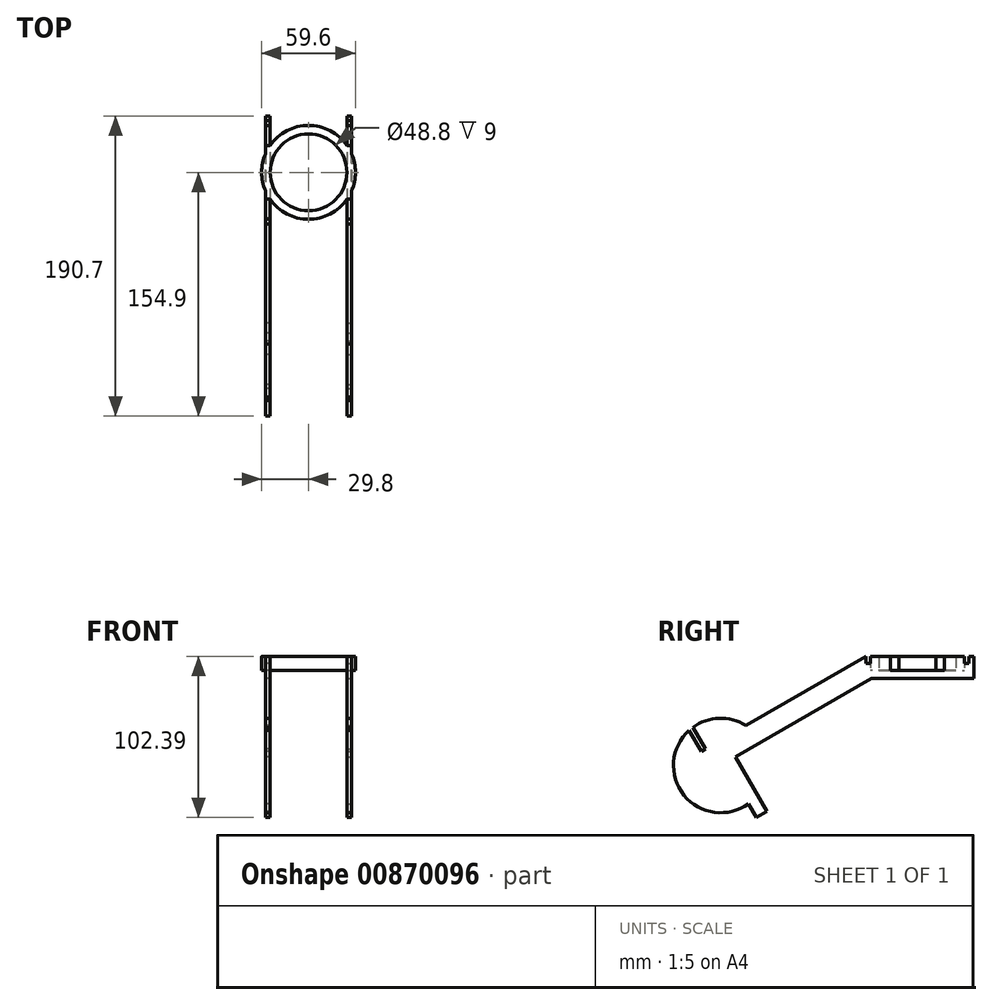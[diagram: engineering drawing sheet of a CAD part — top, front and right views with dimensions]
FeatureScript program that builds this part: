
annotation { "Feature Type Name" : "Feature", "Feature Type Description" : "" }
export const myFeature = defineFeature(function(context is Context, id is Id, definition is map)
    precondition{}
    {
        {
            assignVariable(context, id + "F0", {"name" : "strength", "anyValue" : 3});
        }
        {
            var Q0;
            Q0=qCreatedBy(makeId("Top.planeOp"),FACE);
            var sketch = newSketch(context, id + "F1", { "sketchPlane" : qUnion([Q0])});
            skCircle(sketch, "E0", {"center": v(0, 0) * mm, "radius": 29.8 * mm});
            skCircle(sketch, "E1", {"center": v(0, 0) * mm, "radius": 24.4 * mm});
            skLineSegment(sketch, "E2.bottom", {"start": v(-24.4, -17.1) * mm, "end": v(-27.4, -17.1) * mm});
            skLineSegment(sketch, "E2.top", {"start": v(-24.4, 17.1) * mm, "end": v(-27.4, 17.1) * mm});
            skLineSegment(sketch, "E2.left", {"start": v(-24.4, -17.1) * mm, "end": v(-24.4, 17.1) * mm});
            skLineSegment(sketch, "E2.right", {"start": v(-27.4, -17.1) * mm, "end": v(-27.4, 17.1) * mm});
            skPoint(sketch, "E3", {"position": v(-24.4, -17.1) * mm});
            skPoint(sketch, "E4", {"position": v(-24.4, 17.1) * mm});
            skLineSegment(sketch, "E5.MirrorCS", {"start": v(24.4, 17.1) * mm, "end": v(27.4, 17.1) * mm});
            skLineSegment(sketch, "E6.MirrorCS", {"start": v(27.4, -17.1) * mm, "end": v(27.4, 17.1) * mm});
            skLineSegment(sketch, "E7.MirrorCS", {"start": v(24.4, -17.1) * mm, "end": v(27.4, -17.1) * mm});
            skLineSegment(sketch, "E8.MirrorCS", {"start": v(24.4, -17.1) * mm, "end": v(24.4, 17.1) * mm});
            skSolve(sketch);
        }
        {
            var Q0;
            Q0 = qSketchRegion(id + "F1", true);
            extrude(context, id + "F2", {"entities" : qUnion([Q0]), "depth" : 9 * mm, "offsetDistance" : 25 * mm});
        }
        {
            var Q0;
            {var subQ0=sQuery(id+"F1.wireOp",EDGE,"E2.right");Q0=makeQuery(id+"F2.opExtrude","SWEPT_FACE",FACE,{"disambiguationData":[OSD([subQ0]),TDD([makeQuery(id+"F1.imprint","IMPRINT",EDGE,{"disambiguationData":[TD([[makeQuery(id+"F1.imprint","INTERSECT",VERTEX,{"derivedFrom":[sQuery(id+"F1.wireOp",EDGE,"E2.bottom"),subQ0]}),-1.0]])],"derivedFrom":subQ0})])]});}
            var sketch = newSketch(context, id + "F3", { "sketchPlane" : qUnion([Q0])});
            skLineSegment(sketch, "E9.0", {"start": v(-17.1, 9) * mm, "end": v(-17.1, 0) * mm});
            skLineSegment(sketch, "E10.0", {"start": v(17.1, 9) * mm, "end": v(17.1, 0) * mm});
            skLineSegment(sketch, "E11", {"start": v(-29.8, 0) * mm, "end": v(-29.8, 9) * mm, "construction": true});
            skLineSegment(sketch, "E12", {"start": v(-17.1, 9) * mm, "end": v(-29.8, 9) * mm});
            skLineSegment(sketch, "E13", {"start": v(-29.8, 4.5) * mm, "end": v(-32.8, 4.5) * mm});
            skLineSegment(sketch, "E14", {"start": v(-32.8, 4.5) * mm, "end": v(-32.8, 9) * mm});
            skLineSegment(sketch, "E15", {"start": v(-32.8, 9) * mm, "end": v(-35.8, 9) * mm});
            skLineSegment(sketch, "E16", {"start": v(-35.8, 9) * mm, "end": v(-35.8, 0) * mm});
            skLineSegment(sketch, "E17", {"start": v(-35.8, 0) * mm, "end": v(-35.8, -5) * mm});
            skLineSegment(sketch, "E18", {"start": v(-35.8, -5) * mm, "end": v(29.05, -5) * mm});
            skLineSegment(sketch, "E19", {"start": v(-17.1, 0) * mm, "end": v(0, 0) * mm});
            skLineSegment(sketch, "E20", {"start": v(-29.8, 9) * mm, "end": v(-29.8, 4.5) * mm});
            skLineSegment(sketch, "E21.MirrorCS", {"start": v(17.1, 0) * mm, "end": v(0, 0) * mm});
            skLineSegment(sketch, "E22.MirrorCS", {"start": v(17.1, 9) * mm, "end": v(29.8, 9) * mm});
            skLineSegment(sketch, "E23.MirrorCS", {"start": v(29.8, 4.5) * mm, "end": v(32.8, 4.5) * mm});
            skLineSegment(sketch, "E24.MirrorCS", {"start": v(32.8, 4.5) * mm, "end": v(32.8, 9) * mm});
            skLineSegment(sketch, "E25", {"start": v(29.8, 9) * mm, "end": v(29.8, 4.5) * mm});
            skLineSegment(sketch, "E26", {"start": v(29.05, -5) * mm, "end": v(115.65, -55) * mm});
            skLineSegment(sketch, "E27", {"start": v(115.65, -55) * mm, "end": v(95.65, -89.64) * mm});
            skLineSegment(sketch, "E28", {"start": v(95.65, -89.64) * mm, "end": v(102.15, -93.4) * mm});
            skLineSegment(sketch, "E29", {"start": v(102.15, -93.4) * mm, "end": v(122.15, -58.75) * mm});
            skLineSegment(sketch, "E30", {"start": v(122.15, -58.75) * mm, "end": v(127.65, -61.92) * mm});
            skLineSegment(sketch, "E31", {"start": v(124.9, -60.34) * mm, "end": v(104.9, -94.98) * mm, "construction": true});
            skLineSegment(sketch, "E32", {"start": v(108.92, -34.95) * mm, "end": v(32.8, 9) * mm});
            skLineSegment(sketch, "E33", {"start": v(32.8, 9) * mm, "end": v(32.8, 9) * mm});
            skArc(sketch, "E34", {"start": v(107.23, -84.58) * mm, "mid": v(148.22, -79.2) * mm, "end": v(144.92, -38) * mm});
            skLineSegment(sketch, "E35", {"start": v(127.65, -61.92) * mm, "end": v(134.65, -49.8) * mm, "construction": true});
            skLineSegment(sketch, "E36", {"start": v(108.92, -34.95) * mm, "end": v(134.65, -49.8) * mm, "construction": true});
            skLineSegment(sketch, "E37", {"start": v(134.65, -49.8) * mm, "end": v(142.56, -36.1) * mm});
            skLineSegment(sketch, "E38", {"start": v(134.65, -49.8) * mm, "end": v(137.24, -51.3) * mm});
            skLineSegment(sketch, "E39", {"start": v(137.24, -51.3) * mm, "end": v(144.92, -38) * mm});
            skArc(sketch, "E40.trimOffspring", {"start": v(142.56, -36.1) * mm, "mid": v(118.68, -30.99) * mm, "end": v(98.92, -45.34) * mm});
            skSolve(sketch);
        }
        {
            var Q0;
            Q0 = qSketchRegion(id + "F3", true);
            extrude(context, id + "F4", {"entities" : qUnion([Q0]), "oppositeDirection" : true, "depth" : (getVariable(context, 'strength')) * mm, "offsetDistance" : 25 * mm});
        }
        {
            var Q0;
            Q0=makeQuery(id+"F4.opExtrude","SWEPT_BODY",BODY,{"disambiguationData":[OSD([sQuery(id+"F3.wireOp",EDGE,"E9.0"),sQuery(id+"F3.wireOp",EDGE,"E10.0"),sQuery(id+"F3.wireOp",EDGE,"E12"),sQuery(id+"F3.wireOp",EDGE,"E13"),sQuery(id+"F3.wireOp",EDGE,"E14"),sQuery(id+"F3.wireOp",EDGE,"E15"),sQuery(id+"F3.wireOp",EDGE,"E16"),sQuery(id+"F3.wireOp",EDGE,"E17"),sQuery(id+"F3.wireOp",EDGE,"E18"),sQuery(id+"F3.wireOp",EDGE,"E19"),sQuery(id+"F3.wireOp",EDGE,"E20"),sQuery(id+"F3.wireOp",EDGE,"E21.MirrorCS"),sQuery(id+"F3.wireOp",EDGE,"E22.MirrorCS"),sQuery(id+"F3.wireOp",EDGE,"E23.MirrorCS"),sQuery(id+"F3.wireOp",EDGE,"E24.MirrorCS"),sQuery(id+"F3.wireOp",EDGE,"E25"),sQuery(id+"F3.wireOp",EDGE,"E26"),sQuery(id+"F3.wireOp",EDGE,"E27"),sQuery(id+"F3.wireOp",EDGE,"E28"),sQuery(id+"F3.wireOp",EDGE,"E29"),sQuery(id+"F3.wireOp",EDGE,"E30"),sQuery(id+"F3.wireOp",EDGE,"b50db2fd-4de3-4913-8568-616ec00003a10.MirrorCS"),sQuery(id+"F3.wireOp",EDGE,"11425b02-a189-403f-92d1-50a84b4473e60.MirrorCS"),sQuery(id+"F3.wireOp",EDGE,"6b2a9cb8-ca6a-452a-8801-47c69611852b0.MirrorCS"),sQuery(id+"F3.wireOp",EDGE,"E32"),sQuery(id+"F3.wireOp",EDGE,"IISprHid-dIDS-SGvO-JbBH-AddPjdUraITj")])]});
            var Q1;
            Q1=qCreatedBy(makeId("Right.planeOp"),FACE);
            mirror(context, id + "F5", {"entities" : qUnion([Q0]), "mirrorPlane" : qUnion([Q1])});
        }
    });
